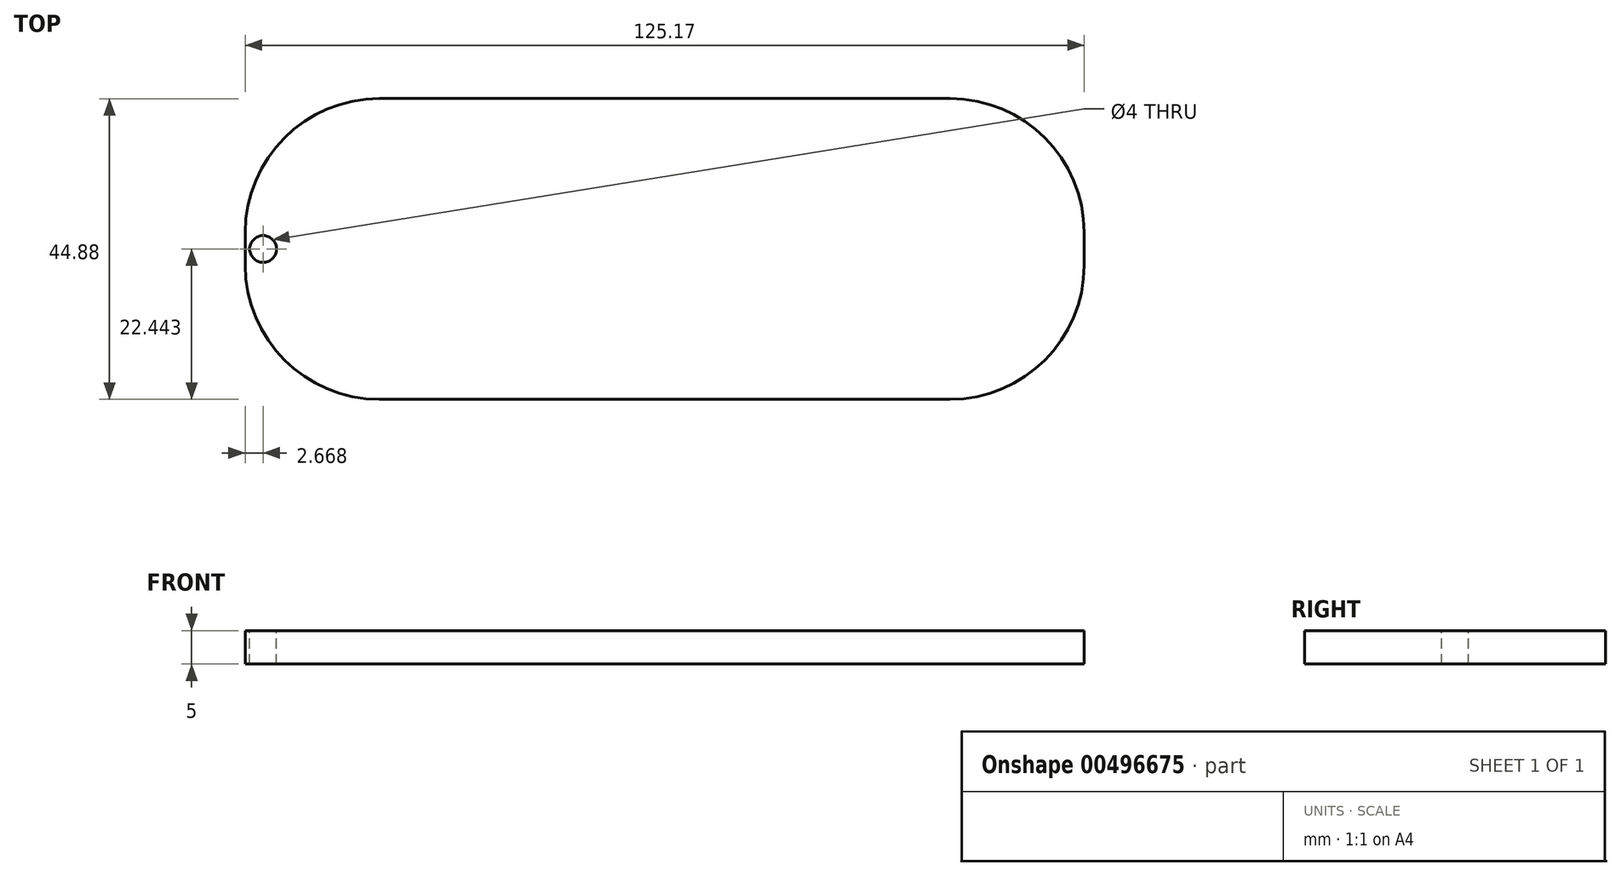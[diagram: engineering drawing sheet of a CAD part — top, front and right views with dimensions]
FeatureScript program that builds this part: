
annotation { "Feature Type Name" : "Feature", "Feature Type Description" : "" }
export const myFeature = defineFeature(function(context is Context, id is Id, definition is map)
    precondition{}
    {
        {
            var Q0;
            Q0=qCreatedBy(makeId("Top.planeOp"),FACE);
            var sketch = newSketch(context, id + "F0", { "sketchPlane" : qUnion([Q0])});
            skLineSegment(sketch, "E0.bottom", {"start": v(-61.66, 24.3) * mm, "end": v(63.51, 24.3) * mm});
            skLineSegment(sketch, "E0.top", {"start": v(-61.66, -20.59) * mm, "end": v(63.51, -20.59) * mm});
            skLineSegment(sketch, "E0.left", {"start": v(-61.66, 24.3) * mm, "end": v(-61.66, -20.59) * mm});
            skLineSegment(sketch, "E0.right", {"start": v(63.51, 24.3) * mm, "end": v(63.51, -20.59) * mm});
            skSolve(sketch);
        }
        {
            var Q0;
            Q0 = qSketchRegion(id + "F0", true);
            extrude(context, id + "F1", {"entities" : qUnion([Q0]), "depth" : 5 * mm, "offsetDistance" : 25 * mm});
        }
        {
            var Q0;
            Q0=makeQuery(id+"F1.opExtrude","SWEPT_EDGE",EDGE,{"disambiguationData":[OSD([sQuery(id+"F0.wireOp",EDGE,"E0.top"),sQuery(id+"F0.wireOp",EDGE,"E0.left")])]});
            var Q1;
            Q1=makeQuery(id+"F1.opExtrude","SWEPT_EDGE",EDGE,{"disambiguationData":[OSD([sQuery(id+"F0.wireOp",EDGE,"E0.bottom"),sQuery(id+"F0.wireOp",EDGE,"E0.left")])]});
            var Q2;
            Q2=makeQuery(id+"F1.opExtrude","SWEPT_EDGE",EDGE,{"disambiguationData":[OSD([sQuery(id+"F0.wireOp",EDGE,"E0.top"),sQuery(id+"F0.wireOp",EDGE,"E0.right")])]});
            var Q3;
            Q3=makeQuery(id+"F1.opExtrude","SWEPT_EDGE",EDGE,{"disambiguationData":[OSD([sQuery(id+"F0.wireOp",EDGE,"E0.bottom"),sQuery(id+"F0.wireOp",EDGE,"E0.right")])]});
            fillet(context, id + "F2", {"entities" : qUnion([Q0, Q1, Q2, Q3]), "radius" : 20 * mm, "tangentPropagation" : true, "allowEdgeOverflow" : false});
        }
        {
            var Q0;
            Q0=makeQuery(id+"F1.opExtrude","CAP_FACE",FACE,{"disambiguationData":[OSD([sQuery(id+"F0.wireOp",EDGE,"E0.bottom"),sQuery(id+"F0.wireOp",EDGE,"E0.top"),sQuery(id+"F0.wireOp",EDGE,"E0.left"),sQuery(id+"F0.wireOp",EDGE,"E0.right")])],"isStart":false});
            var sketch = newSketch(context, id + "F3", { "sketchPlane" : qUnion([Q0])});
            skCircle(sketch, "E1", {"center": v(-59, 1.85) * mm, "radius": 2 * mm});
            skPoint(sketch, "E1.centerSnap0", {"position": v(-61.66, 1.85) * mm});
            skSolve(sketch);
        }
        {
            var Q0;
            Q0 = qSketchRegion(id + "F3", true);
            extrude(context, id + "F4", {"entities" : qUnion([Q0]), "operationType" : NewBodyOperationType.REMOVE, "oppositeDirection" : true, "depth" : 25 * mm, "offsetDistance" : 25 * mm});
        }
    });
